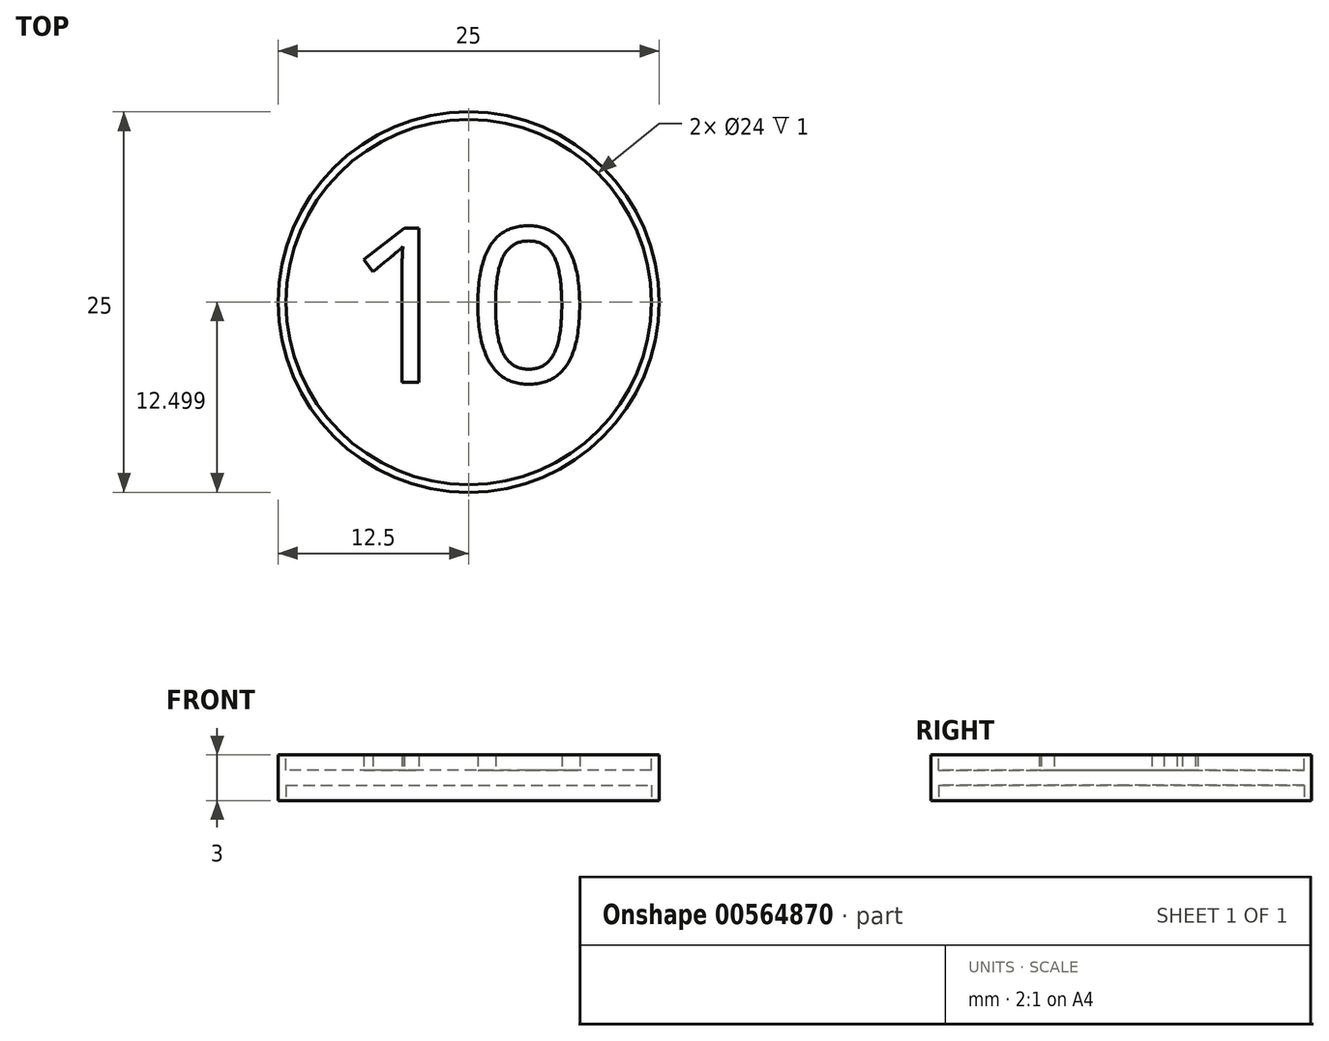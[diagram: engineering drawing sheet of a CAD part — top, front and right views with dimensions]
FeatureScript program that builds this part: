
annotation { "Feature Type Name" : "Feature", "Feature Type Description" : "" }
export const myFeature = defineFeature(function(context is Context, id is Id, definition is map)
    precondition{}
    {
        {
            assignVariable(context, id + "F0", {"name" : "Thickness", "anyValue" : 3});
        }
        {
            assignVariable(context, id + "F1", {"name" : "ImpressionDepth", "anyValue" : 1});
        }
        {
            var Q0;
            Q0=qCreatedBy(makeId("Top.planeOp"),FACE);
            var sketch = newSketch(context, id + "F2", { "sketchPlane" : qUnion([Q0])});
            skCircle(sketch, "E0", {"center": v(0, 0.16) * mm, "radius": 12.5 * mm});
            skSolve(sketch);
        }
        {
            var Q0;
            Q0=qSketchRegion(id+"F2",true);
            var Q1;
            Q1=qConstructionFilter(qBodyType(qCreatedBy(id+"F2",EDGE),BodyType.WIRE),ConstructionObject.NO);
            extrude(context, id + "F3", {"entities" : qUnion([Q0]), "surfaceEntities" : qUnion([Q1]), "depth" : (getVariable(context, 'Thickness')) * mm});
        }
        {
            var Q0;
            Q0=makeQuery(id+"F3.opExtrude","CAP_FACE",FACE,{"disambiguationData":[OSD([sQuery(id+"F2.wireOp",EDGE,"E0")])],"isStart":false});
            var sketch = newSketch(context, id + "F4", { "sketchPlane" : qUnion([Q0])});
            skCircle(sketch, "E1.0", {"center": v(0, 0.16) * mm, "radius": 12 * mm});
            skSolve(sketch);
        }
        {
            var Q0;
            Q0=qSketchRegion(id+"F4",true);
            extrude(context, id + "F5", {"entities" : qUnion([Q0]), "operationType" : NewBodyOperationType.REMOVE, "oppositeDirection" : true, "depth" : (getVariable(context, 'ImpressionDepth')) * mm});
        }
        {
            var Q0;
            Q0=makeQuery(id+"F3.opExtrude","CAP_FACE",FACE,{"disambiguationData":[OSD([sQuery(id+"F2.wireOp",EDGE,"E0")])],"isStart":true});
            var sketch = newSketch(context, id + "F6", { "sketchPlane" : qUnion([Q0])});
            skCircle(sketch, "E2.0", {"center": v(0, -0.16) * mm, "radius": 12 * mm});
            skSolve(sketch);
        }
        {
            var Q0;
            Q0=qSketchRegion(id+"F6",true);
            extrude(context, id + "F7", {"entities" : qUnion([Q0]), "operationType" : NewBodyOperationType.REMOVE, "oppositeDirection" : true, "depth" : (getVariable(context, 'ImpressionDepth')) * mm});
        }
        {
            var Q0;
            Q0=makeQuery(id+"F5.boolean.opBoolean","COPY",FACE,{"derivedFrom":makeQuery(id+"F5.opExtrude","CAP_FACE",FACE,{"disambiguationData":[OSD([sQuery(id+"F4.wireOp",EDGE,"E1.0")])],"isStart":false})});
            var sketch = newSketch(context, id + "F8", { "sketchPlane" : qUnion([Q0])});
            skText(sketch, "E3", { "text": "10", "fontName": "OpenSans-Regular.ttf"});
            skPoint(sketch, "E4", {"position": v(0, 0) * mm});
            const initialGuessF8  = {"E3": [-0.0082, -0.0051, 1, 0, 0.0102]};
            skSetInitialGuess(sketch, initialGuessF8);
            skSolve(sketch);
        }
        {
            var Q0;
            Q0=qSketchRegion(id+"F8",true);
            extrude(context, id + "F9", {"entities" : qUnion([Q0]), "operationType" : NewBodyOperationType.ADD, "depth" : (getVariable(context, 'ImpressionDepth')) * mm});
        }
    });
